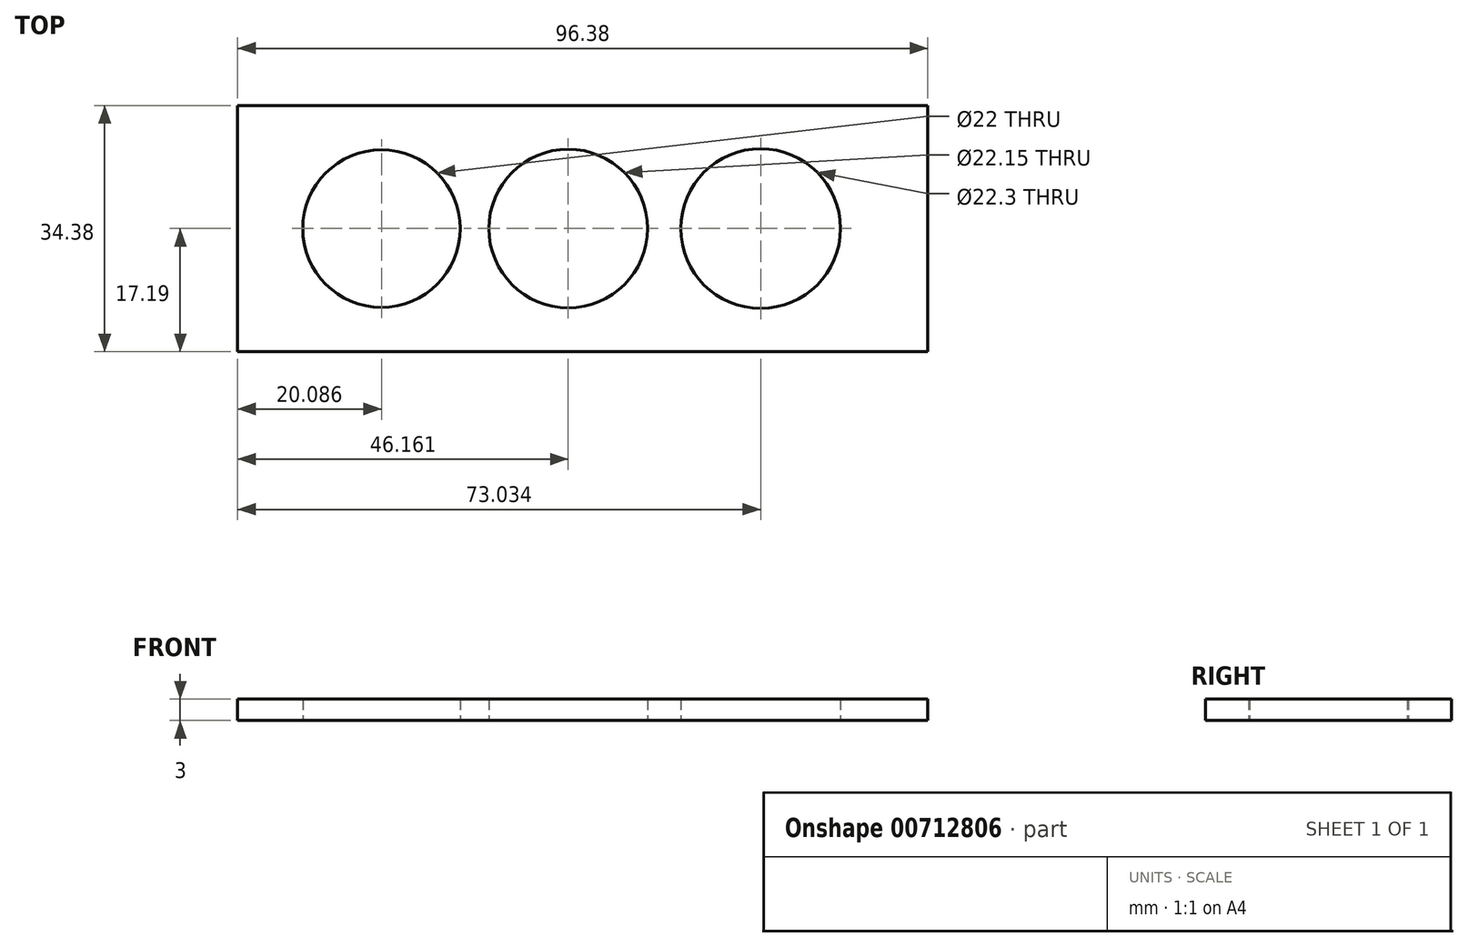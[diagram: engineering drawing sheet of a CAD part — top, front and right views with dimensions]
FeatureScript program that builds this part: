
annotation { "Feature Type Name" : "Feature", "Feature Type Description" : "" }
export const myFeature = defineFeature(function(context is Context, id is Id, definition is map)
    precondition{}
    {
        {
            var Q0;
            Q0=qCreatedBy(makeId("Top.planeOp"),FACE);
            var sketch = newSketch(context, id + "F0", { "sketchPlane" : qUnion([Q0])});
            skLineSegment(sketch, "E0.bottom", {"start": v(-48.19, 17.2) * mm, "end": v(48.19, 17.2) * mm});
            skLineSegment(sketch, "E0.top", {"start": v(-48.19, -17.2) * mm, "end": v(48.19, -17.2) * mm});
            skLineSegment(sketch, "E0.left", {"start": v(-48.19, 17.2) * mm, "end": v(-48.19, -17.2) * mm});
            skLineSegment(sketch, "E0.right", {"start": v(48.19, 17.2) * mm, "end": v(48.19, -17.2) * mm});
            skLineSegment(sketch, "E1", {"start": v(0, 17.2) * mm, "end": v(0, -17.2) * mm, "construction": true});
            skLineSegment(sketch, "E2", {"start": v(-48.19, 0) * mm, "end": v(48.19, 0) * mm, "construction": true});
            skCircle(sketch, "E3", {"center": v(-28.1, 0) * mm, "radius": 11 * mm});
            skCircle(sketch, "E4", {"center": v(-2.03, 0) * mm, "radius": 11.07 * mm});
            skCircle(sketch, "E5", {"center": v(24.84, 0) * mm, "radius": 11.15 * mm});
            skSolve(sketch);
        }
        {
            var Q0;
            Q0=makeQuery(id+"F0.imprint","IMPRINT",FACE,{"disambiguationData":[TD([[makeQuery(id+"F0.imprint","IMPRINT",EDGE,{"derivedFrom":sQuery(id+"F0.wireOp",EDGE,"E0.bottom")}),-1.0]])]});
            extrude(context, id + "F1", {"entities" : qUnion([Q0]), "depth" : 3 * mm, "offsetDistance" : 25 * mm});
        }
    });
